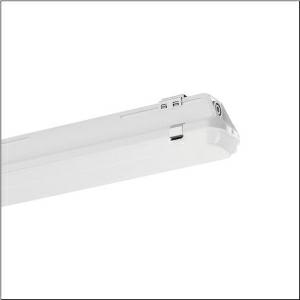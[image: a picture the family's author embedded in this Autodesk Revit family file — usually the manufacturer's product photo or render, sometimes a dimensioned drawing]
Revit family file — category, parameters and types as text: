
# Revit family: monsun_r__21_51fb12mp480c_3942
name_source: partatom
category: Lighting Fixtures
units: mm (PartAtom-declared; Revit-internal decimal feet)

## family parameters
Cut with Voids When Loaded = No
Host = Face
Light Source = No
Part Type = Normal
Room Calculation Point = No
Round Connector Dimension = Use Diameter
Shared = No

## types (1)
- --- (1 x LED, 8380 lm, 45.2 W, 4000K)
    Apparent Load = 45 VA
    CIE Flux Codes = 65 88 97 97 100
    Color Rendering = 80
    Color Temperature = 4000K
    Default Elevation = 1800 mm
    Description = Monsun® 21, damp-proof luminaire, chain hanger, primary light control with lens, primary optical cover: enclosure, of PMMA, light emission: direct distribution, primary light characteristic: symmetric, installation type: suspended mounting, surface-mounted, horizontal mounting, vertical mounting, LED, rated luminous flux: 8.380lm, luminous efficacy: 185lm/W, light colour: 840, colour temperature: 4000K, control gear: ON/OFF Multilumen, with terminal, 3-pole, max. 2.5mm², mains connection: 220..240V, AC, 50/60Hz, rated input power: 45W, housing, of glass-fibre reinforced polyester, uncoated, bright grey, incl. chain hanger, length: 1.590mm, width: 90mm, height: 88mm, clip for enclosure, of stainless steel (V2A), ceiling mounting element, of stainless steel (V2A), chain hanger, of stainless steel (V2A), protection rating (complete): IP66, insulation class (complete): insulation class I (protective earthing), certification: CE, ENEC, VDE, UKCA, protection symbol: D, impact resistance: IK04, permissible operating ambient temperature: -25..+35°C, standard: EN 50419, EN 60598-2-1, contact your sales advisor before using the luminaires in applications with unclear chemical exposure, large temperature fluctuations or condensation-forming humidity, LABS conformity tested according to VDMA 24364:2018-05, no direct snow, no direct sun, no direct rain, for indoor or canopied outdoor use, corresponds to IFS (International Featured Standards) requirements for safety and quality in the food industry, packaging unit: 1 piece
    Height = 89 mm
    Lamp = 1 x LED
    Lamp Light Flux = 8380 lm
    Lamp Power = 45.2 W
    Lamp count = 1
    Length = 1590 mm
    Luminous efficacy = 185 lm/W
    Manufacturer = Siteco
    ModVariant = No
    Model = 51FB12MP480C
    Mounting Place = Ceiling
    Mounting Type = Surface mounted
    Number of Poles = 1
    OnlyDefault = Yes
    Power Factor = 1
    Product Name = Monsun® 21
    Product group = damp-proof luminaire
    ProductGroupID = 300
    Protection Class = Protection class I
    Protection Degree = IP 66
    RLX_Detail_Level = 1
    RLX_Emergency_Light_Flux = 0 lm
    RLX_Emergency_Type = 0
    RLX_Emergency_Type_DB = No
    RlxData = <blob elided: 89905 chars, md5=4fc34f1a>
    Socket = socket
    Standby Power = 0 W
    System Light Flux = 8380 lm
    System Power = 45 W
    Type Comments = factory setting: luminous flux: 100 % | (A | C | E) | 105 mA
    Type Image = l_1319656.jpg
    URL = http://relux.com
    VarID = @adj_042086
    Voltage = 0 V
    Weight = 0.00 kg
    Width = 90 mm

## geometry (parser evidence)
native form markers: Blend x4, Sweep x10
no freeform markers — native parametric forms only
